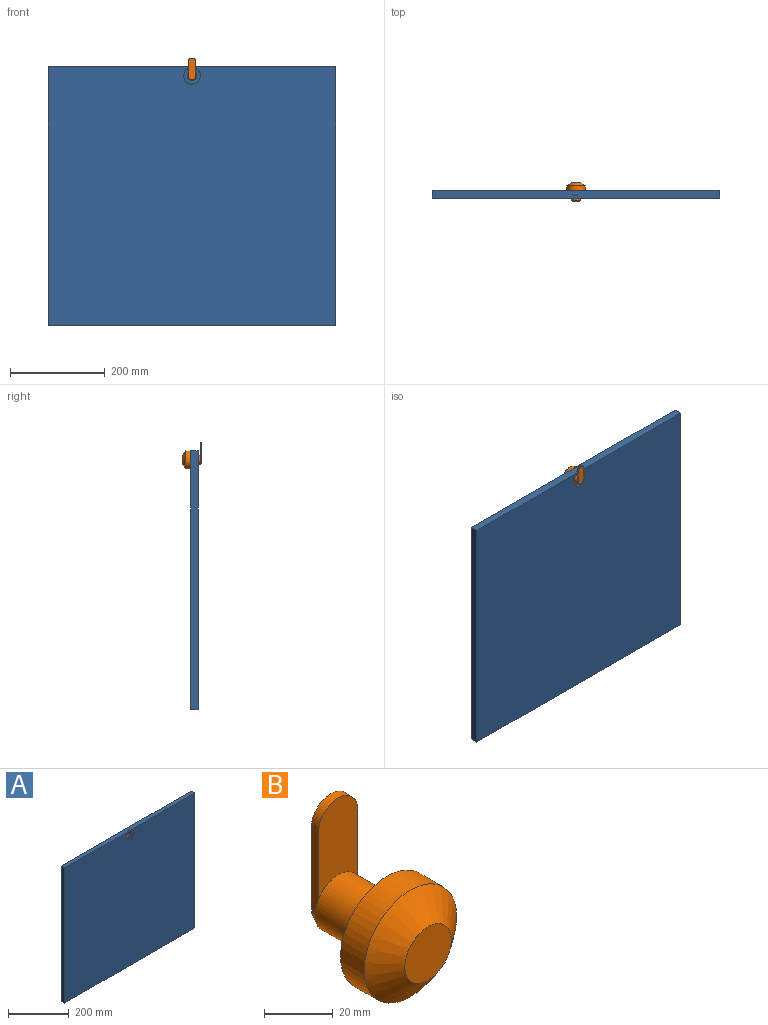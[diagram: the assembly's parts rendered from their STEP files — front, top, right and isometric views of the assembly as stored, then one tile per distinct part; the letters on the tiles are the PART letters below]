
ASSEMBLY  parts=2 mates=1
PART A: 9 faces, bbox 606.6x15.9x545.7 mm
  f0: plane 545.66x15.88mm, normal (-1,0,0), area 8662.4mm2, adj f1,f3,f4,f5
  f1: plane 606.55x545.66mm, normal (0,1,0), area 330664.8mm2, adj f0,f2,f3,f4,f6
  f2: plane 545.66x15.88mm, normal (1,0,0), area 8662.4mm2, adj f1,f3,f4,f5
  f3: plane 606.55x15.88mm, normal (0,0,-1), area 9629mm2, adj f0,f1,f2,f5
  f4: plane 606.55x15.88mm, normal (0,0,1), area 9629mm2, adj f0,f1,f2,f5
  f5: plane 606.55x545.66mm, normal (0,-1,0), area 330016mm2, adj f0,f2,f3,f4,f7
  f6: cylinder r=9.92mm len=19.84mm, axis (0,1,0), area 688.8mm2, adj f1,f8
  f7: cylinder r=17.46mm len=34.93mm, axis (0,-1,0), area 529.5mm2, adj f5,f8
  f8: plane 34.93x34.93mm, normal (0,-1,0), area 648.8mm2, adj f6,f7
PART B: 12 faces, bbox 38x40x56 mm
  f0: plane 19x14.62mm, normal (0,1,0), area 51.7mm2, adj f1,f6,f8,f9
  f1: cylinder r=9.5mm len=20mm, axis (0,-1,0), area 1193.8mm2, adj f0,f2,f11
  f2: plane 38x38mm, normal (0,1,0), area 850.6mm2, adj f1,f3
  f3: cylinder r=19mm len=38mm, axis (0,-1,0), area 1164.8mm2, adj f2,f4
  f4: cone r=9.56mm half-angle=52.5deg, axis (0,1,0), area 1067.6mm2, adj f3,f5
  f5: plane 19.12x19.12mm, normal (0,-1,0), area 287.1mm2, adj f4
  f6: plane 29x3mm, normal (-1,0,0), area 87mm2, adj f0,f7,f9,f10,f11
  f7: cylinder r=8mm len=16mm, axis (0,-1,0), area 75.4mm2, adj f6,f8,f10,f11
  f8: plane 29x3mm, normal (1,0,0), area 87mm2, adj f0,f7,f9,f10,f11
  f9: cylinder r=8mm len=16mm, axis (0,-1,0), area 75.4mm2, adj f0,f6,f8,f10
  f10: plane 45x16mm, normal (0,1,0), area 665.1mm2, adj f6,f7,f8,f9
  f11: plane 31.88x16mm, normal (0,-1,0), area 433.2mm2, adj f1,f6,f7,f8
PLACE A t=(-220.99,-398.22,63.44)mm
PLACE B rot(axis=(0,0,1),180deg) t=(-220.99,-101.27,283.6)mm
MATE fastened B.f1 <-> A.f7  axis (0,1,0) through (-220.99,-99.77,283.6)mm
